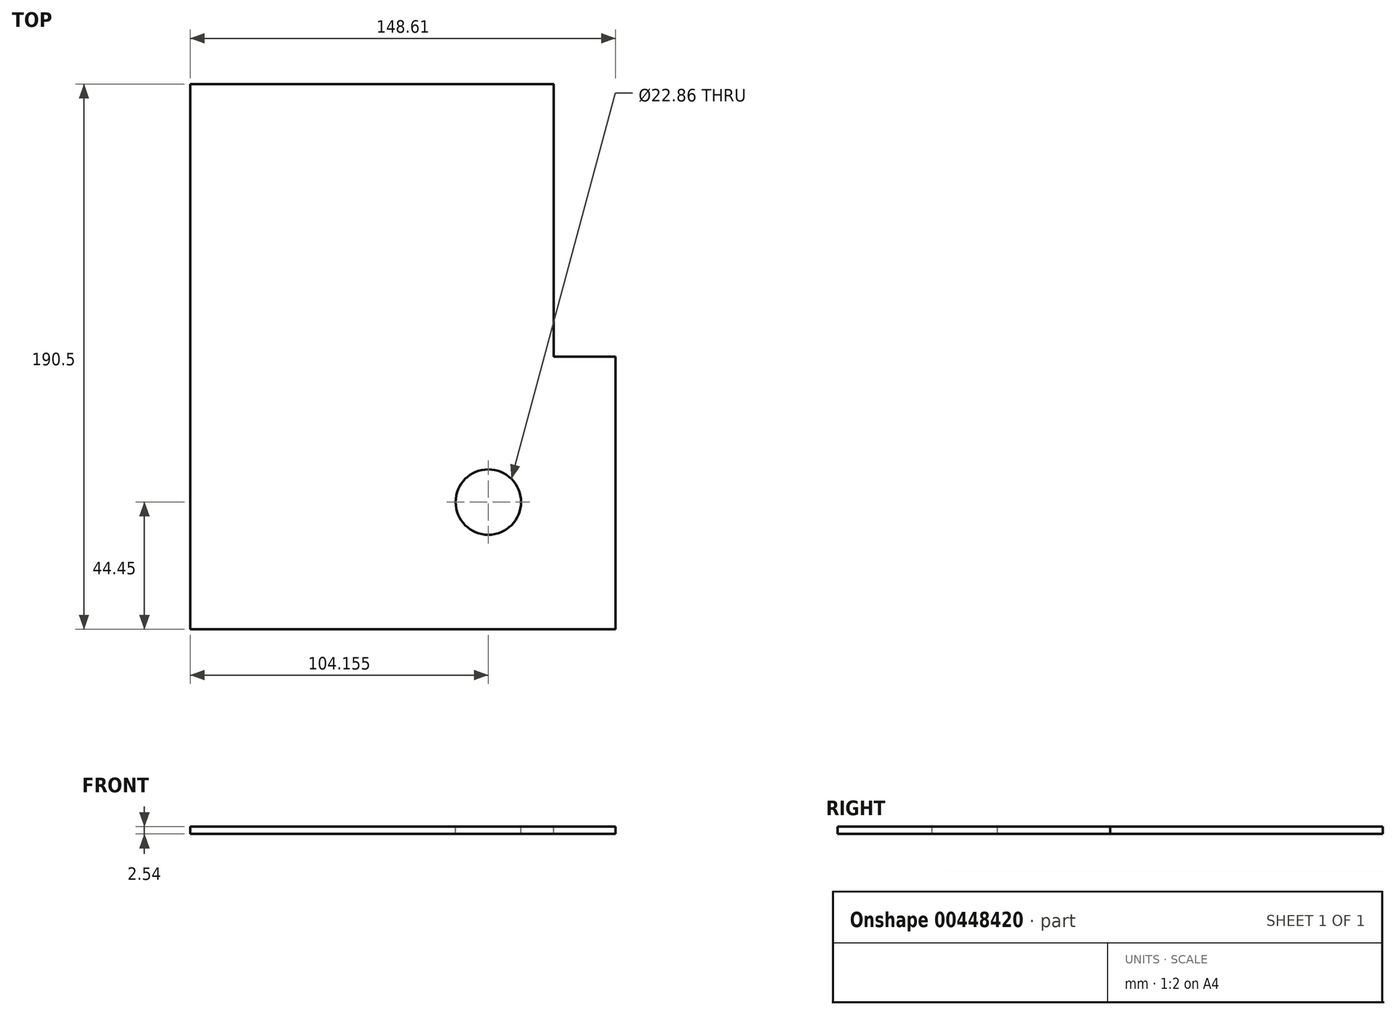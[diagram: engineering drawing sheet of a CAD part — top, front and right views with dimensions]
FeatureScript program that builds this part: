
annotation { "Feature Type Name" : "Feature", "Feature Type Description" : "" }
export const myFeature = defineFeature(function(context is Context, id is Id, definition is map)
    precondition{}
    {
        {
            var Q0;
            Q0=qCreatedBy(makeId("Top.planeOp"),FACE);
            var sketch = newSketch(context, id + "F0", { "sketchPlane" : qUnion([Q0])});
            skLineSegment(sketch, "E0.bottom", {"start": v(63.5, 95.25) * mm, "end": v(-63.5, 95.25) * mm});
            skLineSegment(sketch, "E0.top", {"start": v(63.5, -95.25) * mm, "end": v(-63.5, -95.25) * mm});
            skLineSegment(sketch, "E0.left", {"start": v(63.5, 95.25) * mm, "end": v(63.5, -95.25) * mm});
            skLineSegment(sketch, "E0.right", {"start": v(-63.5, 95.25) * mm, "end": v(-63.5, -95.25) * mm});
            skPoint(sketch, "E0.middle", {"position": v(0, 0) * mm});
            skSolve(sketch);
        }
        {
            var Q0;
            Q0 = qSketchRegion(id + "F0", true);
            extrude(context, id + "F1", {"entities" : qUnion([Q0]), "depth" : 2.54 * mm});
        }
        {
            var Q0;
            Q0=makeQuery(id+"F1.opExtrude","CAP_FACE",FACE,{"disambiguationData":[OSD([sQuery(id+"F0.wireOp",EDGE,"E0.bottom"),sQuery(id+"F0.wireOp",EDGE,"E0.top"),sQuery(id+"F0.wireOp",EDGE,"E0.left"),sQuery(id+"F0.wireOp",EDGE,"E0.right")])],"isStart":false});
            var sketch = newSketch(context, id + "F2", { "sketchPlane" : qUnion([Q0])});
            skLineSegment(sketch, "E1.bottom", {"start": v(63.5, 0) * mm, "end": v(85.1, 0) * mm});
            skLineSegment(sketch, "E1.top", {"start": v(63.5, -95.25) * mm, "end": v(85.1, -95.25) * mm});
            skLineSegment(sketch, "E1.left", {"start": v(63.5, 0) * mm, "end": v(63.5, -95.25) * mm});
            skLineSegment(sketch, "E1.right", {"start": v(85.1, 0) * mm, "end": v(85.1, -95.25) * mm});
            skSolve(sketch);
        }
        {
            var Q0;
            Q0=makeQuery(id+"F2.imprint","IMPRINT",FACE,{"disambiguationData":[TD([[makeQuery(id+"F2.imprint","IMPRINT",EDGE,{"derivedFrom":sQuery(id+"F2.wireOp",EDGE,"E1.bottom")}),-1.0]])]});
            extrude(context, id + "F3", {"entities" : qUnion([Q0]), "operationType" : NewBodyOperationType.ADD, "oppositeDirection" : true, "depth" : 2.54 * mm});
        }
        {
            var Q0;
            Q0=makeQuery(id+"F3.boolean.opBoolean","MERGE",FACE,{"derivedFrom":[makeQuery(id+"F1.opExtrude","CAP_FACE",FACE,{"disambiguationData":[OSD([sQuery(id+"F0.wireOp",EDGE,"E0.bottom"),sQuery(id+"F0.wireOp",EDGE,"E0.top"),sQuery(id+"F0.wireOp",EDGE,"E0.left"),sQuery(id+"F0.wireOp",EDGE,"E0.right")])],"isStart":false}),makeQuery(id+"F3.opExtrude","CAP_FACE",FACE,{"disambiguationData":[OSD([sQuery(id+"F2.wireOp",EDGE,"E1.bottom"),sQuery(id+"F2.wireOp",EDGE,"E1.top"),sQuery(id+"F2.wireOp",EDGE,"E1.left"),sQuery(id+"F2.wireOp",EDGE,"E1.right")])],"isStart":true})]});
            var sketch = newSketch(context, id + "F4", { "sketchPlane" : qUnion([Q0])});
            skCircle(sketch, "E2", {"center": v(40.66, -50.8) * mm, "radius": 12.7 * mm});
            skSolve(sketch);
        }
        {
            var Q0;
            Q0 = qSketchRegion(id + "F4", true);
            extrude(context, id + "F5", {"entities" : qUnion([Q0]), "operationType" : NewBodyOperationType.REMOVE, "oppositeDirection" : true, "depth" : 101.87 * mm});
        }
        {
            var Q0;
            Q0=makeQuery(id+"F3.boolean.opBoolean","MERGE",FACE,{"derivedFrom":[makeQuery(id+"F1.opExtrude","CAP_FACE",FACE,{"disambiguationData":[OSD([sQuery(id+"F0.wireOp",EDGE,"E0.bottom"),sQuery(id+"F0.wireOp",EDGE,"E0.top"),sQuery(id+"F0.wireOp",EDGE,"E0.left"),sQuery(id+"F0.wireOp",EDGE,"E0.right")])],"isStart":false}),makeQuery(id+"F3.opExtrude","CAP_FACE",FACE,{"disambiguationData":[OSD([sQuery(id+"F2.wireOp",EDGE,"E1.bottom"),sQuery(id+"F2.wireOp",EDGE,"E1.top"),sQuery(id+"F2.wireOp",EDGE,"E1.left"),sQuery(id+"F2.wireOp",EDGE,"E1.right")])],"isStart":true})]});
            var sketch = newSketch(context, id + "F6", { "sketchPlane" : qUnion([Q0])});
            skCircle(sketch, "E3", {"center": v(40.66, -50.8) * mm, "radius": 11.43 * mm});
            skSolve(sketch);
        }
        {
            var Q0;
            Q0=makeQuery(id+"F6.imprint","IMPRINT",FACE,{"disambiguationData":[TD([[makeQuery(id+"F6.imprint","IMPRINT",EDGE,{"derivedFrom":sQuery(id+"F6.wireOp",EDGE,"E3")}),-1.0]])]});
            extrude(context, id + "F7", {"entities" : qUnion([Q0]), "operationType" : NewBodyOperationType.ADD, "oppositeDirection" : true, "depth" : 2.54 * mm});
        }
    });
